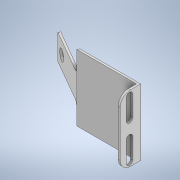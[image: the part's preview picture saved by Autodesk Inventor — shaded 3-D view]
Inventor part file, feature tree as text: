
AUTODESK INVENTOR PART (.ipt)
format: ipt  version: 2021.3 (Build 253353000, 353)  size: 179,200 bytes
history: native  units: mm
features: sketch x5, extrude x4, fillet x2, hole x1
ambient origin geometry x8: Origin, YZ Plane, XZ Plane, XY Plane, X Axis, Y Axis, Z Axis, Center Point
bodies: Volumenkörper1 (feature_tree)
feature tree (12):
  extrude  "Extrusion1"  Depth=2.0mm
  extrude  "Extrusion2"  TaperAngle=150.0deg  [1 undecoded]
  sketch  "Skizze3"  dims[d4=2.0mm d6=65.0mm d7=0.0mm]
  hole  "Bohrung2"  [1 undecoded]
  extrude  "Extrusion3"  Depth=65.0mm
  fillet  "Rundung1"  Radius=18.0mm
  extrude  "Extrusion4"  Depth=4.0mm
  fillet  "Rundung2"  Radius=10.0mm
  sketch  "Skizze1"  dims[d0=2.0mm d1=60.0mm]
  sketch  "Skizze2"  dims[d2=50.0mm d3=150.0deg]
  sketch  "Skizze4"  dims[d8=2.0mm d9=65.0mm d10=18.0mm d11=0.0mm]
  sketch  "Skizze6"  dims[d12=36.0mm d23=32.5mm d24=10.0mm d25=10.4mm d26=6.0mm d27=4.0mm d28=2.0mm d29=90.0deg d30=8.0mm d31=20.594885mm d32=6.2mm d34=20.0mm d35=14.5mm d36=6.2mm d37=20.0mm d38=10.0mm d39=0.0mm d42=0.0mm d43=9.0mm d44=18.0mm d45=10.0mm d46=50.536mm d47=20.0mm d48=50.536mm d49=20.0mm d50=10.0mm d51=0.0mm d52=4.0mm]
note: 2 required parameter values undecoded (feature->parameter linkage not recoverable at this tier; creation-order binding heuristic only, values carry confidence <= 0.55)
